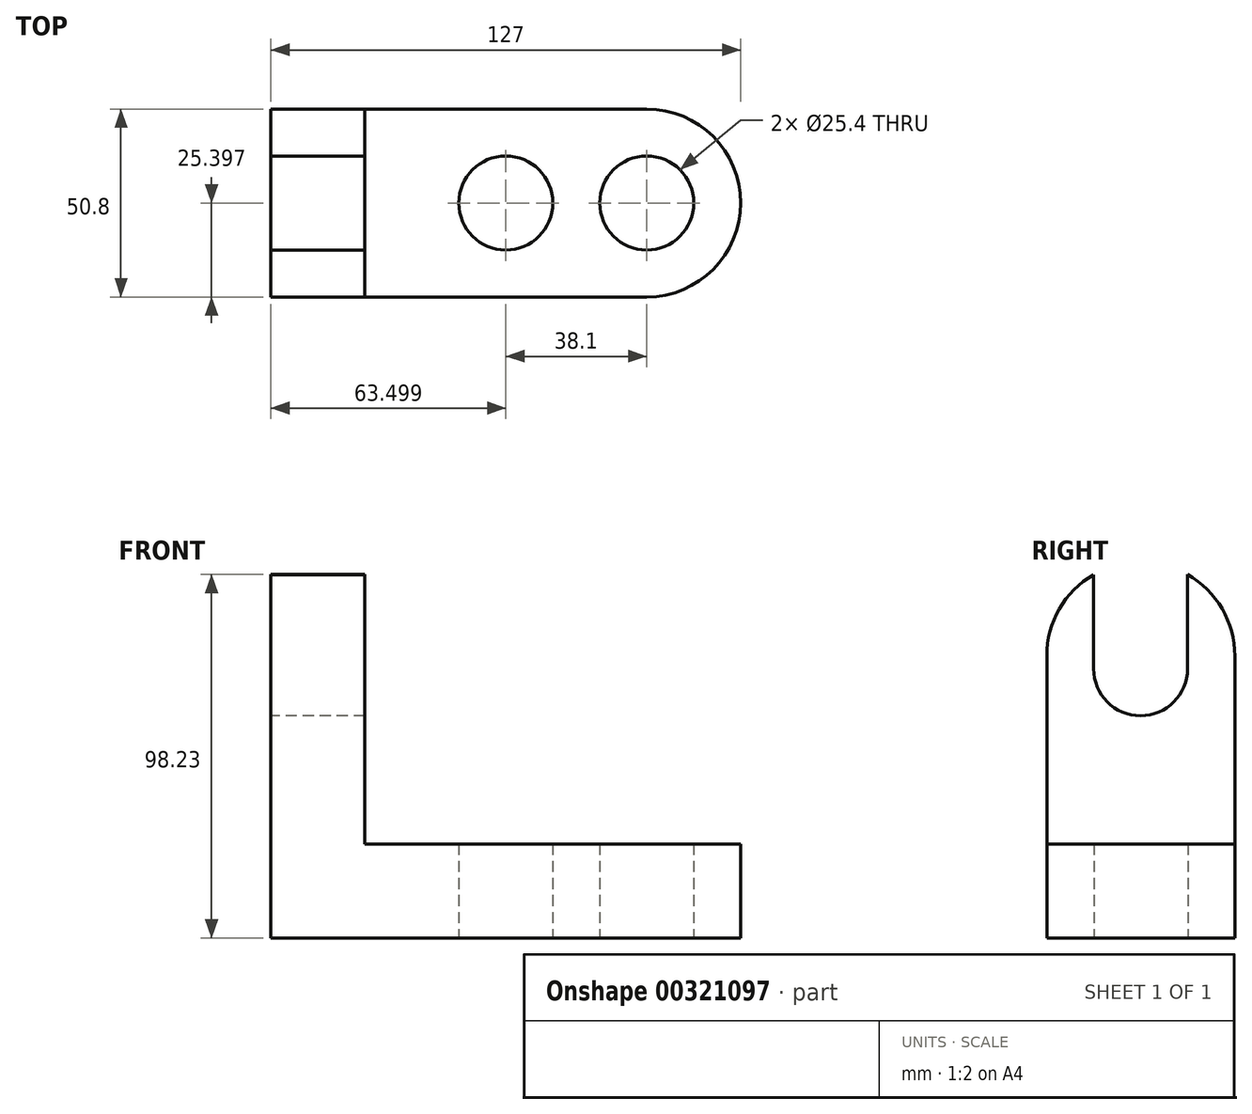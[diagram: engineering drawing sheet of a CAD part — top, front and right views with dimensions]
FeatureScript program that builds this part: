
annotation { "Feature Type Name" : "Feature", "Feature Type Description" : "" }
export const myFeature = defineFeature(function(context is Context, id is Id, definition is map)
    precondition{}
    {
        {
            var Q0;
            Q0=qCreatedBy(makeId("Top.planeOp"),FACE);
            var sketch = newSketch(context, id + "F0", { "sketchPlane" : qUnion([Q0])});
            skLineSegment(sketch, "E0", {"start": v(-44.4, 38.34) * mm, "end": v(57.2, 38.34) * mm});
            skLineSegment(sketch, "E1", {"start": v(-44.4, 38.34) * mm, "end": v(-44.4, -12.46) * mm});
            skLineSegment(sketch, "E2", {"start": v(-44.4, -12.46) * mm, "end": v(57.2, -12.46) * mm});
            skArc(sketch, "E3", {"start": v(57.2, -12.46) * mm, "mid": v(82.6, 12.94) * mm, "end": v(57.2, 38.34) * mm});
            skCircle(sketch, "E4", {"center": v(57.2, 12.94) * mm, "radius": 12.7 * mm});
            skCircle(sketch, "E5", {"center": v(19.1, 12.94) * mm, "radius": 12.7 * mm});
            skSolve(sketch);
        }
        {
            var Q0;
            Q0=makeQuery(id+"F0.imprint","IMPRINT",FACE,{"disambiguationData":[TD([[makeQuery(id+"F0.imprint","IMPRINT",EDGE,{"derivedFrom":sQuery(id+"F0.wireOp",EDGE,"E0")}),-1.0]])]});
            extrude(context, id + "F1", {"entities" : qUnion([Q0]), "depth" : 25.4 * mm});
        }
        {
            var Q0;
            Q0=makeQuery(id+"F1.opExtrude","CAP_FACE",FACE,{"disambiguationData":[OSD([sQuery(id+"F0.wireOp",EDGE,"E0"),sQuery(id+"F0.wireOp",EDGE,"E1"),sQuery(id+"F0.wireOp",EDGE,"E2"),sQuery(id+"F0.wireOp",EDGE,"E3"),sQuery(id+"F0.wireOp",EDGE,"E4"),sQuery(id+"F0.wireOp",EDGE,"E5")])],"isStart":false});
            var sketch = newSketch(context, id + "F2", { "sketchPlane" : qUnion([Q0])});
            skLineSegment(sketch, "E6.bottom", {"start": v(-44.4, -12.46) * mm, "end": v(-19, -12.46) * mm});
            skLineSegment(sketch, "E6.top", {"start": v(-44.4, 38.34) * mm, "end": v(-19, 38.34) * mm});
            skLineSegment(sketch, "E6.left", {"start": v(-44.4, -12.46) * mm, "end": v(-44.4, 38.34) * mm});
            skLineSegment(sketch, "E6.right", {"start": v(-19, -12.46) * mm, "end": v(-19, 38.34) * mm});
            skSolve(sketch);
        }
        {
            var Q0;
            Q0=makeQuery(id+"F2.imprint","IMPRINT",FACE,{"disambiguationData":[TD([[makeQuery(id+"F2.imprint","IMPRINT",EDGE,{"derivedFrom":sQuery(id+"F2.wireOp",EDGE,"E6.bottom")}),1.0]])]});
            extrude(context, id + "F3", {"entities" : qUnion([Q0]), "operationType" : NewBodyOperationType.ADD, "depth" : 76.2 * mm});
        }
        {
            var Q0;
            Q0=makeQuery(id+"F3.opExtrude","CAP_EDGE",EDGE,{"disambiguationData":[OSD([sQuery(id+"F2.wireOp",EDGE,"E6.bottom")])],"isStart":false});
            fillet(context, id + "F4", {"entities" : qUnion([Q0]), "radius" : 25.4 * mm, "tangentPropagation" : true, "allowEdgeOverflow" : false});
        }
        {
            var Q0;
            Q0=makeQuery(id+"F3.opExtrude","CAP_EDGE",EDGE,{"disambiguationData":[OSD([sQuery(id+"F2.wireOp",EDGE,"E6.top")])],"isStart":false});
            fillet(context, id + "F5", {"entities" : qUnion([Q0]), "radius" : 25.4 * mm, "tangentPropagation" : true, "allowEdgeOverflow" : false});
        }
        {
            var Q0;
            Q0=makeQuery(id+"F3.opExtrude","SWEPT_FACE",FACE,{"disambiguationData":[OSD([sQuery(id+"F2.wireOp",EDGE,"E6.right")])]});
            var sketch = newSketch(context, id + "F6", { "sketchPlane" : qUnion([Q0])});
            skLineSegment(sketch, "E7", {"start": v(0.18, 98.16) * mm, "end": v(0.18, 60.06) * mm});
            skLineSegment(sketch, "E8", {"start": v(0.18, 60.06) * mm, "end": v(25.58, 60.06) * mm});
            skLineSegment(sketch, "E9", {"start": v(25.58, 60.06) * mm, "end": v(25.58, 98.23) * mm});
            skSolve(sketch);
        }
        {
            var Q0;
            {var subQ4=sQuery(id+"F6.wireOp",EDGE,"E7");Q0=makeQuery(id+"F6.imprint","IMPRINT",FACE,{"disambiguationData":[TD([[makeQuery(id+"F6.imprint","IMPRINT",EDGE,{"derivedFrom":subQ4}),1.0]])]});}
            extrude(context, id + "F7", {"entities" : qUnion([Q0]), "operationType" : NewBodyOperationType.REMOVE, "endBound" : BoundingType.THROUGH_ALL, "oppositeDirection" : true, "depth" : 25.4 * mm});
        }
        {
            var Q0;
            Q0=makeQuery(id+"F7.boolean.opBoolean","COPY",EDGE,{"derivedFrom":makeQuery(id+"F7.opExtrude","SWEPT_EDGE",EDGE,{"disambiguationData":[OSD([sQuery(id+"F6.wireOp",EDGE,"E7"),sQuery(id+"F6.wireOp",EDGE,"E8")])]})});
            fillet(context, id + "F8", {"entities" : qUnion([Q0]), "radius" : 12.7 * mm, "tangentPropagation" : true, "allowEdgeOverflow" : false});
        }
        {
            var Q0;
            Q0=makeQuery(id+"F7.boolean.opBoolean","COPY",EDGE,{"derivedFrom":makeQuery(id+"F7.opExtrude","SWEPT_EDGE",EDGE,{"disambiguationData":[OSD([sQuery(id+"F6.wireOp",EDGE,"E8"),sQuery(id+"F6.wireOp",EDGE,"E9")])]})});
            fillet(context, id + "F9", {"entities" : qUnion([Q0]), "radius" : 12.7 * mm, "tangentPropagation" : true, "allowEdgeOverflow" : false});
        }
    });
